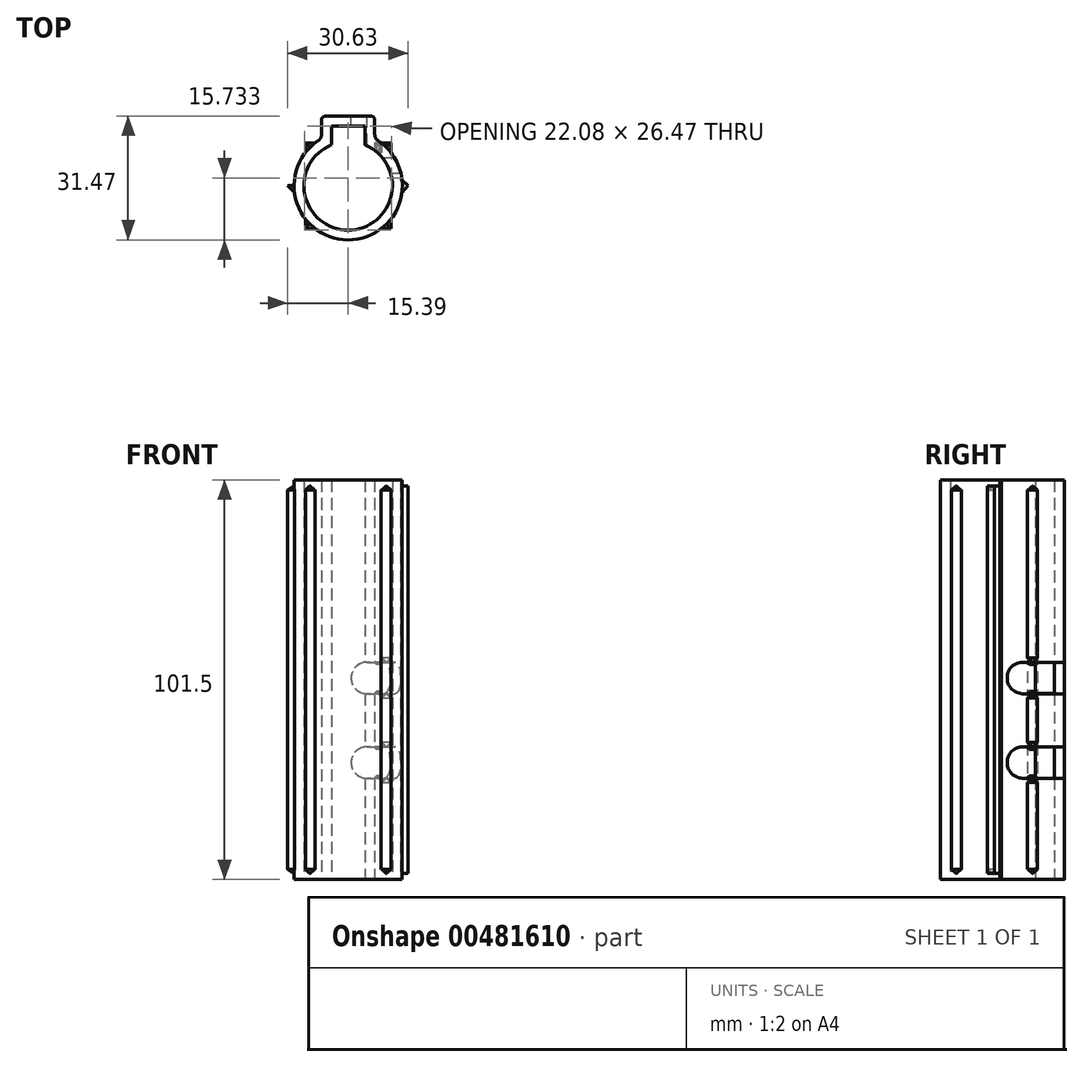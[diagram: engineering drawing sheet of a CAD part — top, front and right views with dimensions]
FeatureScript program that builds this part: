
annotation { "Feature Type Name" : "Feature", "Feature Type Description" : "" }
export const myFeature = defineFeature(function(context is Context, id is Id, definition is map)
    precondition{}
    {
        {
            var Q0;
            Q0=qCreatedBy(makeId("Top.planeOp"),FACE);
            var sketch = newSketch(context, id + "F0", { "sketchPlane" : qUnion([Q0])});
            skArc(sketch, "E0", {"start": v(-4.25, 10.42) * mm, "mid": v(0, -11.25) * mm, "end": v(4.25, 10.42) * mm});
            skLineSegment(sketch, "E1.bottom", {"start": v(-4.25, 15.22) * mm, "end": v(4.25, 15.22) * mm});
            skLineSegment(sketch, "E1.left", {"start": v(-4.25, 15.22) * mm, "end": v(-4.25, 10.42) * mm});
            skLineSegment(sketch, "E1.right", {"start": v(4.25, 15.22) * mm, "end": v(4.25, 10.42) * mm});
            skPoint(sketch, "E2", {"position": v(4.25, 10.42) * mm});
            skPoint(sketch, "E3", {"position": v(-4.25, 10.42) * mm});
            skArc(sketch, "E4.0", {"start": v(-7.64, 11.43) * mm, "mid": v(0, -13.75) * mm, "end": v(7.64, 11.43) * mm});
            skLineSegment(sketch, "E4.1", {"start": v(-6.75, 16.72) * mm, "end": v(-6.75, 13.1) * mm});
            skLineSegment(sketch, "E4.2", {"start": v(-5.75, 17.72) * mm, "end": v(5.75, 17.72) * mm});
            skLineSegment(sketch, "E4.3", {"start": v(6.75, 16.72) * mm, "end": v(6.75, 13.1) * mm});
            skPoint(sketch, "E5.visualSharp", {"position": v(-6.75, 11.98) * mm});
            skArc(sketch, "E5.filletArc", {"start": v(-7.64, 11.43) * mm, "mid": v(-6.99, 12.15) * mm, "end": v(-6.75, 13.1) * mm});
            skPoint(sketch, "E6.visualSharp", {"position": v(6.75, 11.98) * mm});
            skArc(sketch, "E6.filletArc", {"start": v(6.75, 13.1) * mm, "mid": v(6.99, 12.15) * mm, "end": v(7.64, 11.43) * mm});
            skPoint(sketch, "E7.visualSharp", {"position": v(6.75, 17.72) * mm});
            skArc(sketch, "E7.filletArc", {"start": v(6.75, 16.72) * mm, "mid": v(6.46, 17.42) * mm, "end": v(5.75, 17.72) * mm});
            skPoint(sketch, "E8.visualSharp", {"position": v(-6.75, 17.72) * mm});
            skArc(sketch, "E8.filletArc", {"start": v(-5.75, 17.72) * mm, "mid": v(-6.46, 17.42) * mm, "end": v(-6.75, 16.72) * mm});
            skLineSegment(sketch, "E9", {"start": v(0, 0) * mm, "end": v(-7.95, 7.95) * mm});
            skLineSegment(sketch, "E10", {"start": v(0, 0) * mm, "end": v(-11.25, 0) * mm});
            skLineSegment(sketch, "E11", {"start": v(0, 0) * mm, "end": v(-7.95, -7.95) * mm});
            skLineSegment(sketch, "E12", {"start": v(0, 0) * mm, "end": v(7.95, -7.95) * mm});
            skLineSegment(sketch, "E13", {"start": v(0, 0) * mm, "end": v(11.25, 0) * mm});
            skLineSegment(sketch, "E14", {"start": v(0, 0) * mm, "end": v(7.95, 7.95) * mm});
            skLineSegment(sketch, "E15.0", {"start": v(-1.24, 1.24) * mm, "end": v(-9.1, -6.62) * mm});
            skLineSegment(sketch, "E16.0", {"start": v(1.24, -1.24) * mm, "end": v(-6.62, -9.1) * mm});
            skLineSegment(sketch, "E17.0", {"start": v(-1.24, -1.24) * mm, "end": v(6.62, -9.1) * mm});
            skLineSegment(sketch, "E18.0", {"start": v(1.24, 1.24) * mm, "end": v(9.1, -6.62) * mm});
            skLineSegment(sketch, "E19.0", {"start": v(1.24, -1.24) * mm, "end": v(9.1, 6.62) * mm});
            skLineSegment(sketch, "E20.0", {"start": v(-1.24, 1.24) * mm, "end": v(6.62, 9.1) * mm});
            skLineSegment(sketch, "E21.0", {"start": v(1.24, 1.24) * mm, "end": v(-6.62, 9.1) * mm});
            skLineSegment(sketch, "E22.0", {"start": v(-1.24, -1.24) * mm, "end": v(-9.1, 6.62) * mm});
            skLineSegment(sketch, "E23.0", {"start": v(0, 1.75) * mm, "end": v(-11.11, 1.75) * mm});
            skLineSegment(sketch, "E24.0", {"start": v(0, -1.75) * mm, "end": v(-11.11, -1.75) * mm});
            skLineSegment(sketch, "E25.0", {"start": v(0, -1.75) * mm, "end": v(11.11, -1.75) * mm});
            skLineSegment(sketch, "E26.0", {"start": v(0, 1.75) * mm, "end": v(11.11, 1.75) * mm});
            skLineSegment(sketch, "E27", {"start": v(13.64, -1.75) * mm, "end": v(15.24, 0) * mm});
            skLineSegment(sketch, "E28", {"start": v(15.24, 0) * mm, "end": v(13.32, 1.75) * mm});
            skLineSegment(sketch, "E29", {"start": v(8.4, -10.88) * mm, "end": v(10.88, -10.88) * mm});
            skLineSegment(sketch, "E30", {"start": v(10.88, -10.88) * mm, "end": v(10.88, -8.4) * mm});
            skLineSegment(sketch, "E31", {"start": v(-8.4, -10.88) * mm, "end": v(-10.88, -10.88) * mm});
            skLineSegment(sketch, "E32", {"start": v(-10.88, -10.88) * mm, "end": v(-10.88, -8.4) * mm});
            skLineSegment(sketch, "E33", {"start": v(-13.64, -1.75) * mm, "end": v(-15.4, 0) * mm});
            skLineSegment(sketch, "E34", {"start": v(-15.4, 0) * mm, "end": v(-13.65, 1.75) * mm});
            skLineSegment(sketch, "E35", {"start": v(-10.88, 8.4) * mm, "end": v(-10.88, 10.88) * mm});
            skLineSegment(sketch, "E36", {"start": v(-10.88, 10.88) * mm, "end": v(-8.4, 10.88) * mm});
            skLineSegment(sketch, "E37", {"start": v(8.4, 10.88) * mm, "end": v(10.88, 10.88) * mm});
            skLineSegment(sketch, "E38", {"start": v(10.88, 10.88) * mm, "end": v(10.88, 8.4) * mm});
            skLineSegment(sketch, "E39.trimOffspring", {"start": v(-8.4, -10.88) * mm, "end": v(-11.52, -14) * mm});
            skLineSegment(sketch, "E40.trimOffspring", {"start": v(-9.72, -9.72) * mm, "end": v(-12.76, -12.76) * mm});
            skLineSegment(sketch, "E41.trimOffspring", {"start": v(-10.88, -8.4) * mm, "end": v(-14, -11.52) * mm});
            skLineSegment(sketch, "E42.trimOffspring", {"start": v(-13.64, -1.75) * mm, "end": v(-22.63, -1.75) * mm});
            skLineSegment(sketch, "E43.trimOffspring", {"start": v(-13.75, 0) * mm, "end": v(-22.63, 0) * mm});
            skLineSegment(sketch, "E44.trimOffspring", {"start": v(-13.65, 1.75) * mm, "end": v(-22.63, 1.75) * mm});
            skLineSegment(sketch, "E45.trimOffspring", {"start": v(-10.88, 8.4) * mm, "end": v(-16.1, 13.63) * mm});
            skLineSegment(sketch, "E46.trimOffspring", {"start": v(-9.72, 9.72) * mm, "end": v(-14.87, 14.87) * mm});
            skLineSegment(sketch, "E47.trimOffspring", {"start": v(-8.4, 10.88) * mm, "end": v(-13.63, 16.1) * mm});
            skLineSegment(sketch, "E48.trimOffspring", {"start": v(8.4, 10.88) * mm, "end": v(14.56, 17.03) * mm});
            skLineSegment(sketch, "E49.trimOffspring", {"start": v(9.72, 9.72) * mm, "end": v(15.8, 15.8) * mm});
            skLineSegment(sketch, "E50.trimOffspring", {"start": v(10.88, 8.4) * mm, "end": v(17.03, 14.56) * mm});
            skLineSegment(sketch, "E51.trimOffspring", {"start": v(13.32, 1.75) * mm, "end": v(21.6, 1.75) * mm});
            skLineSegment(sketch, "E52.trimOffspring", {"start": v(13.75, 0) * mm, "end": v(21.6, 0) * mm});
            skLineSegment(sketch, "E53.trimOffspring", {"start": v(13.64, -1.75) * mm, "end": v(21.6, -1.75) * mm});
            skLineSegment(sketch, "E54.trimOffspring", {"start": v(10.88, -8.4) * mm, "end": v(14.6, -12.12) * mm});
            skLineSegment(sketch, "E55.trimOffspring", {"start": v(9.72, -9.72) * mm, "end": v(13.36, -13.36) * mm});
            skLineSegment(sketch, "E56.trimOffspring", {"start": v(8.4, -10.88) * mm, "end": v(12.12, -14.6) * mm});
            skSolve(sketch);
        }
        {
            var Q0;
            Q0=makeQuery(id+"F0.imprint","IMPRINT",FACE,{"disambiguationData":[TD([[makeQuery(id+"F0.imprint","IMPRINT",EDGE,{"derivedFrom":sQuery(id+"F0.wireOp",EDGE,"E0")}),-1.0]])]});
            extrude(context, id + "F1", {"entities" : qUnion([Q0]), "depth" : 101.5 * mm});
        }
        {
            var Q0;
            Q0=makeQuery(id+"F1.opExtrude","SWEPT_FACE",FACE,{"disambiguationData":[OSD([sQuery(id+"F0.wireOp",EDGE,"E4.2")])]});
            var sketch = newSketch(context, id + "F2", { "sketchPlane" : qUnion([Q0])});
            skCircle(sketch, "E57", {"center": v(-4.75, 29.7) * mm, "radius": 4 * mm});
            skCircle(sketch, "E58", {"center": v(-4.75, 51.2) * mm, "radius": 4 * mm});
            skPoint(sketch, "E59", {"position": v(-0.75, 29.7) * mm});
            skPoint(sketch, "E60", {"position": v(-0.75, 51.2) * mm});
            skSolve(sketch);
        }
        {
            var Q0;
            {var subQ0=sQuery(id+"F2.wireOp",EDGE,"E57");var subQ1=makeQuery(id+"F1.opExtrude","SWEPT_EDGE",EDGE,{"disambiguationData":[OSD([sQuery(id+"F0.wireOp",EDGE,"E4.2"),sQuery(id+"F0.wireOp",EDGE,"E7.filletArc")])]});var subQ2=makeQuery(id+"F2.imprint","INTERSECT",VERTEX,{"disambiguationData":[OD(0.0)],"derivedFrom":[subQ1,subQ0]});Q0=makeQuery(id+"F2.imprint","IMPRINT",FACE,{"disambiguationData":[TD([[makeQuery(id+"F2.imprint","IMPRINT",EDGE,{"disambiguationData":[TD([[subQ2,-1.0]])],"derivedFrom":subQ0}),1.0]])]});}
            var Q1;
            {var subQ0=sQuery(id+"F2.wireOp",EDGE,"E57");var subQ1=makeQuery(id+"F1.opExtrude","SWEPT_EDGE",EDGE,{"disambiguationData":[OSD([sQuery(id+"F0.wireOp",EDGE,"E4.2"),sQuery(id+"F0.wireOp",EDGE,"E7.filletArc")])]});var subQ2=makeQuery(id+"F2.imprint","INTERSECT",VERTEX,{"disambiguationData":[OD(0.0)],"derivedFrom":[subQ1,subQ0]});Q1=makeQuery(id+"F2.imprint","IMPRINT",FACE,{"disambiguationData":[TD([[makeQuery(id+"F2.imprint","IMPRINT",EDGE,{"disambiguationData":[TD([[subQ2,1.0]])],"derivedFrom":subQ0}),1.0]])]});}
            var Q2;
            {var subQ0=sQuery(id+"F2.wireOp",EDGE,"E58");var subQ1=makeQuery(id+"F1.opExtrude","SWEPT_EDGE",EDGE,{"disambiguationData":[OSD([sQuery(id+"F0.wireOp",EDGE,"E4.2"),sQuery(id+"F0.wireOp",EDGE,"E7.filletArc")])]});var subQ2=makeQuery(id+"F2.imprint","INTERSECT",VERTEX,{"disambiguationData":[OD(0.0)],"derivedFrom":[subQ1,subQ0]});Q2=makeQuery(id+"F2.imprint","IMPRINT",FACE,{"disambiguationData":[TD([[makeQuery(id+"F2.imprint","IMPRINT",EDGE,{"disambiguationData":[TD([[subQ2,-1.0]])],"derivedFrom":subQ0}),1.0]])]});}
            var Q3;
            {var subQ0=sQuery(id+"F2.wireOp",EDGE,"E58");var subQ1=makeQuery(id+"F1.opExtrude","SWEPT_EDGE",EDGE,{"disambiguationData":[OSD([sQuery(id+"F0.wireOp",EDGE,"E4.2"),sQuery(id+"F0.wireOp",EDGE,"E7.filletArc")])]});var subQ2=makeQuery(id+"F2.imprint","INTERSECT",VERTEX,{"disambiguationData":[OD(0.0)],"derivedFrom":[subQ1,subQ0]});Q3=makeQuery(id+"F2.imprint","IMPRINT",FACE,{"disambiguationData":[TD([[makeQuery(id+"F2.imprint","IMPRINT",EDGE,{"disambiguationData":[TD([[subQ2,1.0]])],"derivedFrom":subQ0}),1.0]])]});}
            extrude(context, id + "F3", {"entities" : qUnion([Q0, Q1, Q2, Q3]), "operationType" : NewBodyOperationType.REMOVE, "oppositeDirection" : true, "depth" : 12.4 * mm});
        }
        {
            var Q0;
            Q0=makeQuery(id+"F3.boolean.opBoolean","SPLIT",FACE,{"disambiguationData":[TD([makeQuery(id+"F1.opExtrude","SWEPT_FACE",FACE,{"disambiguationData":[OSD([sQuery(id+"F0.wireOp",EDGE,"E6.filletArc")])]}),makeQuery(id+"F1.opExtrude","SWEPT_FACE",FACE,{"disambiguationData":[OSD([sQuery(id+"F0.wireOp",EDGE,"E7.filletArc")])]}),makeQuery(id+"F3.opExtrude","SWEPT_FACE",FACE,{"disambiguationData":[OSD([sQuery(id+"F2.wireOp",EDGE,"E57")])]}),makeQuery(id+"F3.opExtrude","SWEPT_FACE",FACE,{"disambiguationData":[OSD([sQuery(id+"F2.wireOp",EDGE,"E58")])]})])],"derivedFrom":makeQuery(id+"F1.opExtrude","SWEPT_FACE",FACE,{"disambiguationData":[OSD([sQuery(id+"F0.wireOp",EDGE,"E4.3")])]})});
            var sketch = newSketch(context, id + "F4", { "sketchPlane" : qUnion([Q0])});
            skArc(sketch, "E61", {"start": v(7.3, 55.2) * mm, "mid": v(3.22, 51.28) * mm, "end": v(7.14, 47.2) * mm});
            skArc(sketch, "E62", {"start": v(7.31, 33.7) * mm, "mid": v(3.22, 29.8) * mm, "end": v(7.12, 25.7) * mm});
            skPoint(sketch, "E63", {"position": v(3.22, 51.2) * mm});
            skPoint(sketch, "E64", {"position": v(3.22, 29.7) * mm});
            skLineSegment(sketch, "E65.bottom", {"start": v(7.14, 55.2) * mm, "end": v(22.13, 55.2) * mm});
            skLineSegment(sketch, "E65.top", {"start": v(7.14, 47.2) * mm, "end": v(22.13, 47.2) * mm});
            skLineSegment(sketch, "E65.left", {"start": v(7.14, 47.2) * mm, "end": v(7.14, 47.2) * mm});
            skLineSegment(sketch, "E65.right", {"start": v(22.13, 55.2) * mm, "end": v(22.13, 47.2) * mm});
            skLineSegment(sketch, "E66.bottom", {"start": v(7.12, 33.7) * mm, "end": v(24.23, 33.7) * mm});
            skLineSegment(sketch, "E66.top", {"start": v(7.12, 25.7) * mm, "end": v(24.23, 25.7) * mm});
            skLineSegment(sketch, "E66.left", {"start": v(7.12, 25.7) * mm, "end": v(7.12, 25.7) * mm});
            skLineSegment(sketch, "E66.right", {"start": v(24.23, 33.7) * mm, "end": v(24.23, 25.7) * mm});
            skSolve(sketch);
        }
        {
            var Q0;
            {var subQ0=sQuery(id+"F0.wireOp",EDGE,"E33");Q0=makeQuery(id+"F0.imprint","IMPRINT",FACE,{"disambiguationData":[TD([[makeQuery(id+"F0.imprint","IMPRINT",EDGE,{"derivedFrom":subQ0}),-1.0]])]});}
            var Q1;
            {var subQ0=sQuery(id+"F0.wireOp",EDGE,"E43.trimOffspring");var subQ1=sQuery(id+"F0.wireOp",EDGE,"E4.0");var subQ2=makeQuery(id+"F0.imprint","INTERSECT",VERTEX,{"derivedFrom":[subQ1,subQ0]});Q1=makeQuery(id+"F0.imprint","IMPRINT",FACE,{"disambiguationData":[TD([[makeQuery(id+"F0.imprint","IMPRINT",EDGE,{"disambiguationData":[TD([[subQ2,1.0]])],"derivedFrom":subQ1}),-1.0]])]});}
            var Q2;
            {var subQ0=sQuery(id+"F0.wireOp",EDGE,"E32");Q2=makeQuery(id+"F0.imprint","IMPRINT",FACE,{"disambiguationData":[TD([[makeQuery(id+"F0.imprint","IMPRINT",EDGE,{"derivedFrom":subQ0}),-1.0]])]});}
            var Q3;
            {var subQ0=sQuery(id+"F0.wireOp",EDGE,"E31");Q3=makeQuery(id+"F0.imprint","IMPRINT",FACE,{"disambiguationData":[TD([[makeQuery(id+"F0.imprint","IMPRINT",EDGE,{"derivedFrom":subQ0}),-1.0]])]});}
            var Q4;
            {var subQ0=sQuery(id+"F0.wireOp",EDGE,"E29");Q4=makeQuery(id+"F0.imprint","IMPRINT",FACE,{"disambiguationData":[TD([[makeQuery(id+"F0.imprint","IMPRINT",EDGE,{"derivedFrom":subQ0}),1.0]])]});}
            var Q5;
            {var subQ0=sQuery(id+"F0.wireOp",EDGE,"E30");Q5=makeQuery(id+"F0.imprint","IMPRINT",FACE,{"disambiguationData":[TD([[makeQuery(id+"F0.imprint","IMPRINT",EDGE,{"derivedFrom":subQ0}),1.0]])]});}
            var Q6;
            {var subQ0=sQuery(id+"F0.wireOp",EDGE,"E27");Q6=makeQuery(id+"F0.imprint","IMPRINT",FACE,{"disambiguationData":[TD([[makeQuery(id+"F0.imprint","IMPRINT",EDGE,{"derivedFrom":subQ0}),1.0]])]});}
            var Q7;
            {var subQ0=sQuery(id+"F0.wireOp",EDGE,"E52.trimOffspring");var subQ1=sQuery(id+"F0.wireOp",EDGE,"E4.0");var subQ2=makeQuery(id+"F0.imprint","INTERSECT",VERTEX,{"derivedFrom":[subQ1,subQ0]});Q7=makeQuery(id+"F0.imprint","IMPRINT",FACE,{"disambiguationData":[TD([[makeQuery(id+"F0.imprint","IMPRINT",EDGE,{"disambiguationData":[TD([[subQ2,-1.0]])],"derivedFrom":subQ1}),-1.0]])]});}
            var Q8;
            {var subQ0=sQuery(id+"F0.wireOp",EDGE,"E38");Q8=makeQuery(id+"F0.imprint","IMPRINT",FACE,{"disambiguationData":[TD([[makeQuery(id+"F0.imprint","IMPRINT",EDGE,{"derivedFrom":subQ0}),-1.0]])]});}
            var Q9;
            {var subQ0=sQuery(id+"F0.wireOp",EDGE,"E37");Q9=makeQuery(id+"F0.imprint","IMPRINT",FACE,{"disambiguationData":[TD([[makeQuery(id+"F0.imprint","IMPRINT",EDGE,{"derivedFrom":subQ0}),-1.0]])]});}
            var Q10;
            {var subQ0=sQuery(id+"F0.wireOp",EDGE,"E36");Q10=makeQuery(id+"F0.imprint","IMPRINT",FACE,{"disambiguationData":[TD([[makeQuery(id+"F0.imprint","IMPRINT",EDGE,{"derivedFrom":subQ0}),-1.0]])]});}
            var Q11;
            {var subQ0=sQuery(id+"F0.wireOp",EDGE,"E35");Q11=makeQuery(id+"F0.imprint","IMPRINT",FACE,{"disambiguationData":[TD([[makeQuery(id+"F0.imprint","IMPRINT",EDGE,{"derivedFrom":subQ0}),-1.0]])]});}
            extrude(context, id + "F5", {"entities" : qUnion([Q0, Q1, Q2, Q3, Q4, Q5, Q6, Q7, Q8, Q9, Q10, Q11]), "depth" : 100 * mm, "hasSecondDirection" : true, "secondDirectionOppositeDirection" : false, "secondDirectionDepth" : 1.5 * mm});
        }
        {
            var Q0;
            Q0=makeQuery(id+"F4.imprint","IMPRINT",FACE,{"disambiguationData":[TD([[makeQuery(id+"F4.imprint","IMPRINT",EDGE,{"derivedFrom":sQuery(id+"F4.wireOp",EDGE,"E66.top")}),1.0]])]});
            var Q1;
            {var subQ1=sQuery(id+"F0.wireOp",EDGE,"E4.3");var subQ2=makeQuery(id+"F1.opExtrude","SWEPT_FACE",FACE,{"disambiguationData":[OSD([subQ1])]});var subQ5=makeQuery(id+"F3.opExtrude","SWEPT_FACE",FACE,{"disambiguationData":[OSD([sQuery(id+"F2.wireOp",EDGE,"E57")])]});var subQ11=makeQuery(id+"F3.boolean.opBoolean","INTERSECT",EDGE,{"disambiguationData":[OD(1.0)],"derivedFrom":[subQ2,subQ5]});Q1=makeQuery(id+"F4.imprint","IMPRINT",FACE,{"disambiguationData":[TD([[makeQuery(id+"F4.imprint","IMPRINT",EDGE,{"derivedFrom":subQ11}),-1.0]])]});}
            var Q2;
            {var subQ5=sQuery(id+"F4.wireOp",EDGE,"E65.left");Q2=makeQuery(id+"F4.imprint","IMPRINT",FACE,{"disambiguationData":[TD([[makeQuery(id+"F4.imprint","IMPRINT",EDGE,{"derivedFrom":subQ5}),1.0]])]});}
            var Q3;
            {var subQ1=sQuery(id+"F0.wireOp",EDGE,"E4.3");var subQ2=makeQuery(id+"F1.opExtrude","SWEPT_FACE",FACE,{"disambiguationData":[OSD([subQ1])]});var subQ3=makeQuery(id+"F3.opExtrude","SWEPT_FACE",FACE,{"disambiguationData":[OSD([sQuery(id+"F2.wireOp",EDGE,"E58")])]});var subQ11=makeQuery(id+"F3.boolean.opBoolean","INTERSECT",EDGE,{"disambiguationData":[OD(1.0)],"derivedFrom":[subQ2,subQ3]});Q3=makeQuery(id+"F4.imprint","IMPRINT",FACE,{"disambiguationData":[TD([[makeQuery(id+"F4.imprint","IMPRINT",EDGE,{"derivedFrom":subQ11}),-1.0]])]});}
            extrude(context, id + "F6", {"entities" : qUnion([Q0, Q1, Q2, Q3]), "operationType" : NewBodyOperationType.REMOVE, "oppositeDirection" : true, "depth" : 2 * mm, "hasSecondDirection" : true, "secondDirectionOppositeDirection" : false, "secondDirectionDepth" : 25 * mm});
        }
        {
            var Q0;
            {var subQ6=sQuery(id+"F4.wireOp",EDGE,"E66.top");Q0=makeQuery(id+"F6.boolean.opBoolean","COPY",FACE,{"disambiguationData":[TD([makeQuery(id+"F1.opExtrude","SWEPT_FACE",FACE,{"disambiguationData":[OSD([sQuery(id+"F0.wireOp",EDGE,"E0")])]})])],"derivedFrom":makeQuery(id+"F6.opExtrude","SWEPT_FACE",FACE,{"disambiguationData":[OSD([subQ6])]})});}
            var sketch = newSketch(context, id + "F7", { "sketchPlane" : qUnion([Q0])});
            skPoint(sketch, "E67", {"position": v(8.46, 10.84) * mm});
            skLineSegment(sketch, "E68.bottom", {"start": v(8.46, 10.84) * mm, "end": v(6.76, 10.84) * mm});
            skLineSegment(sketch, "E68.top", {"start": v(8.46, 8.4) * mm, "end": v(6.76, 8.4) * mm});
            skLineSegment(sketch, "E68.left", {"start": v(8.46, 10.84) * mm, "end": v(8.46, 8.4) * mm});
            skLineSegment(sketch, "E68.right", {"start": v(6.76, 10.84) * mm, "end": v(6.76, 8.4) * mm});
            skSolve(sketch);
        }
        {
            var Q0;
            Q0=makeQuery(id+"F6.boolean.opBoolean","COPY",FACE,{"disambiguationData":[TD([makeQuery(id+"F1.opExtrude","SWEPT_FACE",FACE,{"disambiguationData":[OSD([sQuery(id+"F0.wireOp",EDGE,"E0")])]})])],"derivedFrom":makeQuery(id+"F6.opExtrude","SWEPT_FACE",FACE,{"disambiguationData":[OSD([sQuery(id+"F4.wireOp",EDGE,"E66.bottom")])]})});
            var sketch = newSketch(context, id + "F8", { "sketchPlane" : qUnion([Q0])});
            skPoint(sketch, "E69", {"position": v(8.46, -10.84) * mm});
            skLineSegment(sketch, "E70.bottom", {"start": v(8.46, -10.84) * mm, "end": v(6.76, -10.84) * mm});
            skLineSegment(sketch, "E70.top", {"start": v(8.46, -8.4) * mm, "end": v(6.76, -8.4) * mm});
            skLineSegment(sketch, "E70.left", {"start": v(8.46, -10.84) * mm, "end": v(8.46, -8.4) * mm});
            skLineSegment(sketch, "E70.right", {"start": v(6.76, -10.84) * mm, "end": v(6.76, -8.4) * mm});
            skSolve(sketch);
        }
        {
            var Q0;
            {var subQ6=sQuery(id+"F4.wireOp",EDGE,"E65.top");Q0=makeQuery(id+"F6.boolean.opBoolean","COPY",FACE,{"disambiguationData":[TD([makeQuery(id+"F1.opExtrude","SWEPT_FACE",FACE,{"disambiguationData":[OSD([sQuery(id+"F0.wireOp",EDGE,"E0")])]})])],"derivedFrom":makeQuery(id+"F6.opExtrude","SWEPT_FACE",FACE,{"disambiguationData":[OSD([subQ6])]})});}
            var sketch = newSketch(context, id + "F9", { "sketchPlane" : qUnion([Q0])});
            skPoint(sketch, "E71", {"position": v(8.45, 10.85) * mm});
            skLineSegment(sketch, "E72.bottom", {"start": v(8.45, 10.85) * mm, "end": v(6.75, 10.85) * mm});
            skLineSegment(sketch, "E72.top", {"start": v(8.45, 8.4) * mm, "end": v(6.75, 8.4) * mm});
            skLineSegment(sketch, "E72.left", {"start": v(8.45, 10.85) * mm, "end": v(8.45, 8.4) * mm});
            skLineSegment(sketch, "E72.right", {"start": v(6.75, 10.85) * mm, "end": v(6.75, 8.4) * mm});
            skSolve(sketch);
        }
        {
            var Q0;
            Q0=makeQuery(id+"F6.boolean.opBoolean","COPY",FACE,{"disambiguationData":[TD([makeQuery(id+"F1.opExtrude","SWEPT_FACE",FACE,{"disambiguationData":[OSD([sQuery(id+"F0.wireOp",EDGE,"E0")])]})])],"derivedFrom":makeQuery(id+"F6.opExtrude","SWEPT_FACE",FACE,{"disambiguationData":[OSD([sQuery(id+"F4.wireOp",EDGE,"E65.bottom")])]})});
            var sketch = newSketch(context, id + "F10", { "sketchPlane" : qUnion([Q0])});
            skPoint(sketch, "E73", {"position": v(8.45, -10.84) * mm});
            skLineSegment(sketch, "E74.bottom", {"start": v(8.45, -10.84) * mm, "end": v(6.75, -10.84) * mm});
            skLineSegment(sketch, "E74.top", {"start": v(8.45, -8.4) * mm, "end": v(6.75, -8.4) * mm});
            skLineSegment(sketch, "E74.left", {"start": v(8.45, -10.84) * mm, "end": v(8.45, -8.4) * mm});
            skLineSegment(sketch, "E74.right", {"start": v(6.75, -10.84) * mm, "end": v(6.75, -8.4) * mm});
            skSolve(sketch);
        }
        {
            var Q0;
            Q0=makeQuery(id+"F10.imprint","IMPRINT",FACE,{"disambiguationData":[TD([[makeQuery(id+"F10.imprint","IMPRINT",EDGE,{"derivedFrom":sQuery(id+"F10.wireOp",EDGE,"E74.bottom")}),-1.0]])]});
            var Q1;
            Q1=makeQuery(id+"F8.imprint","IMPRINT",FACE,{"disambiguationData":[TD([[makeQuery(id+"F8.imprint","IMPRINT",EDGE,{"derivedFrom":sQuery(id+"F8.wireOp",EDGE,"E70.bottom")}),-1.0]])]});
            extrude(context, id + "F11", {"entities" : qUnion([Q0, Q1]), "operationType" : NewBodyOperationType.ADD, "depth" : 0.6 * mm});
        }
        {
            var Q0;
            Q0=makeQuery(id+"F9.imprint","IMPRINT",FACE,{"disambiguationData":[TD([[makeQuery(id+"F9.imprint","IMPRINT",EDGE,{"derivedFrom":sQuery(id+"F9.wireOp",EDGE,"E72.bottom")}),1.0]])]});
            var Q1;
            Q1=makeQuery(id+"F7.imprint","IMPRINT",FACE,{"disambiguationData":[TD([[makeQuery(id+"F7.imprint","IMPRINT",EDGE,{"derivedFrom":sQuery(id+"F7.wireOp",EDGE,"E68.bottom")}),1.0]])]});
            extrude(context, id + "F12", {"entities" : qUnion([Q0, Q1]), "operationType" : NewBodyOperationType.ADD, "depth" : 0.6 * mm});
        }
        {
            var Q0;
            Q0=makeQuery(id+"F11.opExtrude","CAP_EDGE",EDGE,{"disambiguationData":[OSD([sQuery(id+"F10.wireOp",EDGE,"E74.bottom")])],"isStart":false});
            var Q1;
            Q1=makeQuery(id+"F11.opExtrude","CAP_EDGE",EDGE,{"disambiguationData":[OSD([sQuery(id+"F10.wireOp",EDGE,"E74.left")])],"isStart":false});
            var Q2;
            Q2=makeQuery(id+"F11.opExtrude","CAP_EDGE",EDGE,{"disambiguationData":[OSD([sQuery(id+"F10.wireOp",EDGE,"E74.top")])],"isStart":false});
            var Q3;
            Q3=makeQuery(id+"F11.opExtrude","CAP_EDGE",EDGE,{"disambiguationData":[OSD([sQuery(id+"F10.wireOp",EDGE,"E74.right")])],"isStart":false});
            var Q4;
            Q4=makeQuery(id+"F12.opExtrude","CAP_EDGE",EDGE,{"disambiguationData":[OSD([sQuery(id+"F9.wireOp",EDGE,"E72.right")])],"isStart":false});
            var Q5;
            Q5=makeQuery(id+"F12.opExtrude","CAP_EDGE",EDGE,{"disambiguationData":[OSD([sQuery(id+"F9.wireOp",EDGE,"E72.bottom")])],"isStart":false});
            var Q6;
            Q6=makeQuery(id+"F12.opExtrude","CAP_EDGE",EDGE,{"disambiguationData":[OSD([sQuery(id+"F9.wireOp",EDGE,"E72.left")])],"isStart":false});
            var Q7;
            Q7=makeQuery(id+"F12.opExtrude","CAP_EDGE",EDGE,{"disambiguationData":[OSD([sQuery(id+"F9.wireOp",EDGE,"E72.top")])],"isStart":false});
            var Q8;
            Q8=makeQuery(id+"F11.opExtrude","CAP_EDGE",EDGE,{"disambiguationData":[OSD([sQuery(id+"F8.wireOp",EDGE,"E70.bottom")])],"isStart":false});
            var Q9;
            Q9=makeQuery(id+"F11.opExtrude","CAP_EDGE",EDGE,{"disambiguationData":[OSD([sQuery(id+"F8.wireOp",EDGE,"E70.right")])],"isStart":false});
            var Q10;
            Q10=makeQuery(id+"F11.opExtrude","CAP_EDGE",EDGE,{"disambiguationData":[OSD([sQuery(id+"F8.wireOp",EDGE,"E70.left")])],"isStart":false});
            var Q11;
            Q11=makeQuery(id+"F11.opExtrude","CAP_EDGE",EDGE,{"disambiguationData":[OSD([sQuery(id+"F8.wireOp",EDGE,"E70.top")])],"isStart":false});
            var Q12;
            Q12=makeQuery(id+"F12.opExtrude","CAP_EDGE",EDGE,{"disambiguationData":[OSD([sQuery(id+"F7.wireOp",EDGE,"E68.left")])],"isStart":false});
            var Q13;
            Q13=makeQuery(id+"F12.opExtrude","CAP_EDGE",EDGE,{"disambiguationData":[OSD([sQuery(id+"F7.wireOp",EDGE,"E68.bottom")])],"isStart":false});
            var Q14;
            Q14=makeQuery(id+"F12.opExtrude","CAP_EDGE",EDGE,{"disambiguationData":[OSD([sQuery(id+"F7.wireOp",EDGE,"E68.right")])],"isStart":false});
            var Q15;
            Q15=makeQuery(id+"F12.opExtrude","CAP_EDGE",EDGE,{"disambiguationData":[OSD([sQuery(id+"F7.wireOp",EDGE,"E68.top")])],"isStart":false});
            chamfer(context, id + "F13", {"entities" : qUnion([Q0, Q1, Q2, Q3, Q4, Q5, Q6, Q7, Q8, Q9, Q10, Q11, Q12, Q13, Q14, Q15]), "width" : 0.5 * mm, "tangentPropagation" : true});
        }
        {
            var Q0;
            Q0=makeQuery(id+"F5.opExtrude","CAP_EDGE",EDGE,{"disambiguationData":[OSD([sQuery(id+"F0.wireOp",EDGE,"E30")])],"isStart":false});
            var Q1;
            Q1=makeQuery(id+"F5.opExtrude","CAP_EDGE",EDGE,{"disambiguationData":[OSD([sQuery(id+"F0.wireOp",EDGE,"E29")])],"isStart":false});
            var Q2;
            Q2=makeQuery(id+"F5.opExtrude","CAP_EDGE",EDGE,{"disambiguationData":[OSD([sQuery(id+"F0.wireOp",EDGE,"E27")])],"isStart":false});
            var Q3;
            Q3=makeQuery(id+"F5.opExtrude","CAP_EDGE",EDGE,{"disambiguationData":[OSD([sQuery(id+"F0.wireOp",EDGE,"E28")])],"isStart":false});
            var Q4;
            Q4=makeQuery(id+"F5.opExtrude","CAP_EDGE",EDGE,{"disambiguationData":[OSD([sQuery(id+"F0.wireOp",EDGE,"E37")])],"isStart":false});
            var Q5;
            Q5=makeQuery(id+"F5.opExtrude","CAP_EDGE",EDGE,{"disambiguationData":[OSD([sQuery(id+"F0.wireOp",EDGE,"E38")])],"isStart":false});
            var Q6;
            Q6=makeQuery(id+"F5.opExtrude","CAP_EDGE",EDGE,{"disambiguationData":[OSD([sQuery(id+"F0.wireOp",EDGE,"E36")])],"isStart":false});
            var Q7;
            Q7=makeQuery(id+"F5.opExtrude","CAP_EDGE",EDGE,{"disambiguationData":[OSD([sQuery(id+"F0.wireOp",EDGE,"E35")])],"isStart":false});
            var Q8;
            Q8=makeQuery(id+"F5.opExtrude","CAP_EDGE",EDGE,{"disambiguationData":[OSD([sQuery(id+"F0.wireOp",EDGE,"E34")])],"isStart":false});
            var Q9;
            Q9=makeQuery(id+"F5.opExtrude","CAP_EDGE",EDGE,{"disambiguationData":[OSD([sQuery(id+"F0.wireOp",EDGE,"E33")])],"isStart":false});
            var Q10;
            Q10=makeQuery(id+"F5.opExtrude","CAP_EDGE",EDGE,{"disambiguationData":[OSD([sQuery(id+"F0.wireOp",EDGE,"E32")])],"isStart":false});
            var Q11;
            Q11=makeQuery(id+"F5.opExtrude","CAP_EDGE",EDGE,{"disambiguationData":[OSD([sQuery(id+"F0.wireOp",EDGE,"E31")])],"isStart":false});
            var Q12;
            Q12=makeQuery(id+"F5.opExtrude","CAP_EDGE",EDGE,{"disambiguationData":[OSD([sQuery(id+"F0.wireOp",EDGE,"E32")])],"isStart":true});
            var Q13;
            Q13=makeQuery(id+"F5.opExtrude","CAP_EDGE",EDGE,{"disambiguationData":[OSD([sQuery(id+"F0.wireOp",EDGE,"E31")])],"isStart":true});
            var Q14;
            Q14=makeQuery(id+"F5.opExtrude","CAP_EDGE",EDGE,{"disambiguationData":[OSD([sQuery(id+"F0.wireOp",EDGE,"E33")])],"isStart":true});
            var Q15;
            Q15=makeQuery(id+"F5.opExtrude","CAP_EDGE",EDGE,{"disambiguationData":[OSD([sQuery(id+"F0.wireOp",EDGE,"E34")])],"isStart":true});
            var Q16;
            Q16=makeQuery(id+"F5.opExtrude","CAP_EDGE",EDGE,{"disambiguationData":[OSD([sQuery(id+"F0.wireOp",EDGE,"E35")])],"isStart":true});
            var Q17;
            Q17=makeQuery(id+"F5.opExtrude","CAP_EDGE",EDGE,{"disambiguationData":[OSD([sQuery(id+"F0.wireOp",EDGE,"E36")])],"isStart":true});
            var Q18;
            Q18=makeQuery(id+"F5.opExtrude","CAP_EDGE",EDGE,{"disambiguationData":[OSD([sQuery(id+"F0.wireOp",EDGE,"E29")])],"isStart":true});
            var Q19;
            Q19=makeQuery(id+"F5.opExtrude","CAP_EDGE",EDGE,{"disambiguationData":[OSD([sQuery(id+"F0.wireOp",EDGE,"E30")])],"isStart":true});
            var Q20;
            Q20=makeQuery(id+"F5.opExtrude","CAP_EDGE",EDGE,{"disambiguationData":[OSD([sQuery(id+"F0.wireOp",EDGE,"E27")])],"isStart":true});
            var Q21;
            Q21=makeQuery(id+"F5.opExtrude","CAP_EDGE",EDGE,{"disambiguationData":[OSD([sQuery(id+"F0.wireOp",EDGE,"E28")])],"isStart":true});
            var Q22;
            Q22=makeQuery(id+"F5.opExtrude","CAP_EDGE",EDGE,{"disambiguationData":[OSD([sQuery(id+"F0.wireOp",EDGE,"E38")])],"isStart":true});
            var Q23;
            Q23=makeQuery(id+"F5.opExtrude","CAP_EDGE",EDGE,{"disambiguationData":[OSD([sQuery(id+"F0.wireOp",EDGE,"E37")])],"isStart":true});
            var Q24;
            Q24=makeQuery(id+"F6.boolean.opBoolean","INTERSECT",EDGE,{"derivedFrom":[makeQuery(id+"F5.opExtrude","SWEPT_FACE",FACE,{"disambiguationData":[OSD([sQuery(id+"F0.wireOp",EDGE,"E38")])]}),makeQuery(id+"F6.opExtrude","SWEPT_FACE",FACE,{"disambiguationData":[OSD([sQuery(id+"F4.wireOp",EDGE,"E66.top")])]})]});
            var Q25;
            Q25=makeQuery(id+"F6.boolean.opBoolean","INTERSECT",EDGE,{"derivedFrom":[makeQuery(id+"F5.opExtrude","SWEPT_FACE",FACE,{"disambiguationData":[OSD([sQuery(id+"F0.wireOp",EDGE,"E37")])]}),makeQuery(id+"F6.opExtrude","SWEPT_FACE",FACE,{"disambiguationData":[OSD([sQuery(id+"F4.wireOp",EDGE,"E66.top")])]})]});
            var Q26;
            Q26=makeQuery(id+"F6.boolean.opBoolean","INTERSECT",EDGE,{"derivedFrom":[makeQuery(id+"F5.opExtrude","SWEPT_FACE",FACE,{"disambiguationData":[OSD([sQuery(id+"F0.wireOp",EDGE,"E38")])]}),makeQuery(id+"F6.opExtrude","SWEPT_FACE",FACE,{"disambiguationData":[OSD([sQuery(id+"F4.wireOp",EDGE,"E66.bottom")])]})]});
            var Q27;
            Q27=makeQuery(id+"F6.boolean.opBoolean","INTERSECT",EDGE,{"derivedFrom":[makeQuery(id+"F5.opExtrude","SWEPT_FACE",FACE,{"disambiguationData":[OSD([sQuery(id+"F0.wireOp",EDGE,"E37")])]}),makeQuery(id+"F6.opExtrude","SWEPT_FACE",FACE,{"disambiguationData":[OSD([sQuery(id+"F4.wireOp",EDGE,"E66.bottom")])]})]});
            var Q28;
            Q28=makeQuery(id+"F6.boolean.opBoolean","INTERSECT",EDGE,{"derivedFrom":[makeQuery(id+"F5.opExtrude","SWEPT_FACE",FACE,{"disambiguationData":[OSD([sQuery(id+"F0.wireOp",EDGE,"E38")])]}),makeQuery(id+"F6.opExtrude","SWEPT_FACE",FACE,{"disambiguationData":[OSD([sQuery(id+"F4.wireOp",EDGE,"E65.top")])]})]});
            var Q29;
            Q29=makeQuery(id+"F6.boolean.opBoolean","INTERSECT",EDGE,{"derivedFrom":[makeQuery(id+"F5.opExtrude","SWEPT_FACE",FACE,{"disambiguationData":[OSD([sQuery(id+"F0.wireOp",EDGE,"E37")])]}),makeQuery(id+"F6.opExtrude","SWEPT_FACE",FACE,{"disambiguationData":[OSD([sQuery(id+"F4.wireOp",EDGE,"E65.top")])]})]});
            var Q30;
            Q30=makeQuery(id+"F6.boolean.opBoolean","INTERSECT",EDGE,{"derivedFrom":[makeQuery(id+"F5.opExtrude","SWEPT_FACE",FACE,{"disambiguationData":[OSD([sQuery(id+"F0.wireOp",EDGE,"E38")])]}),makeQuery(id+"F6.opExtrude","SWEPT_FACE",FACE,{"disambiguationData":[OSD([sQuery(id+"F4.wireOp",EDGE,"E65.bottom")])]})]});
            var Q31;
            Q31=makeQuery(id+"F6.boolean.opBoolean","INTERSECT",EDGE,{"derivedFrom":[makeQuery(id+"F5.opExtrude","SWEPT_FACE",FACE,{"disambiguationData":[OSD([sQuery(id+"F0.wireOp",EDGE,"E37")])]}),makeQuery(id+"F6.opExtrude","SWEPT_FACE",FACE,{"disambiguationData":[OSD([sQuery(id+"F4.wireOp",EDGE,"E65.bottom")])]})]});
            chamfer(context, id + "F14", {"entities" : qUnion([Q0, Q1, Q2, Q3, Q4, Q5, Q6, Q7, Q8, Q9, Q10, Q11, Q12, Q13, Q14, Q15, Q16, Q17, Q18, Q19, Q20, Q21, Q22, Q23, Q24, Q25, Q26, Q27, Q28, Q29, Q30, Q31]), "width" : 1.1 * mm, "tangentPropagation" : true});
        }
    });
